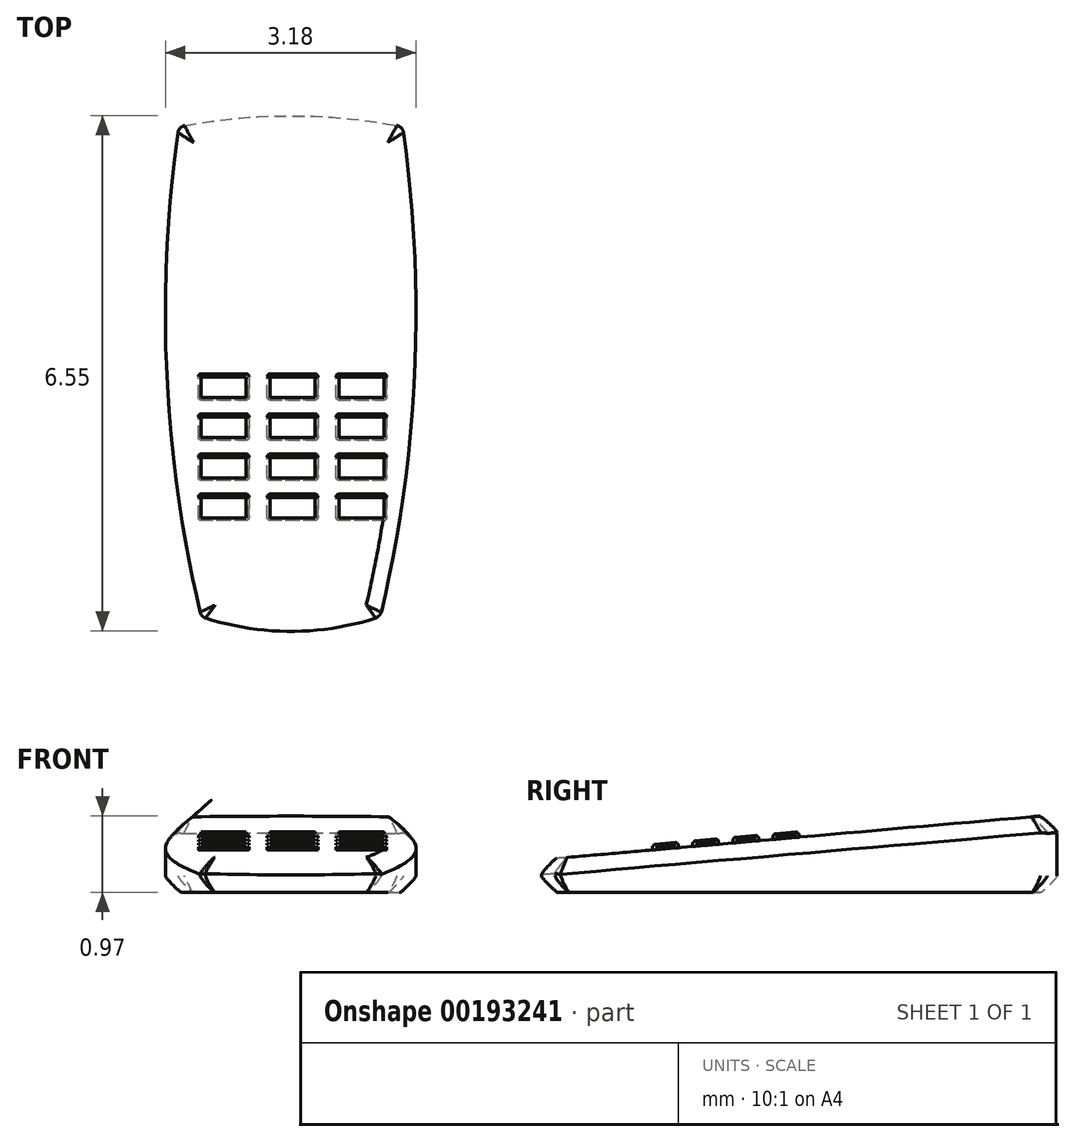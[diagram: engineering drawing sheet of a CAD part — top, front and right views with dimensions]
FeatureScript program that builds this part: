
annotation { "Feature Type Name" : "Feature", "Feature Type Description" : "" }
export const myFeature = defineFeature(function(context is Context, id is Id, definition is map)
    precondition{}
    {
        {
            var Q0;
            Q0=qCreatedBy(makeId("Top.planeOp"),FACE);
            var sketch = newSketch(context, id + "F0", { "sketchPlane" : qUnion([Q0])});
            skPoint(sketch, "E0", {"position": v(-40.64, 114.48) * mm});
            skPoint(sketch, "E1", {"position": v(-32.5, -63.32) * mm});
            skPoint(sketch, "E2.MirrorP", {"position": v(40.64, 114.48) * mm});
            skPoint(sketch, "E3.MirrorP", {"position": v(32.5, -63.32) * mm});
            skArc(sketch, "E4", {"start": v(38.52, 114.88) * mm, "mid": v(0, 118.42) * mm, "end": v(-38.52, 114.88) * mm});
            skArc(sketch, "E5", {"start": v(-40.94, 112.35) * mm, "mid": v(-45, 24.95) * mm, "end": v(-32.89, -61.7) * mm});
            skArc(sketch, "E6", {"start": v(-30.9, -63.86) * mm, "mid": v(0, -68.73) * mm, "end": v(30.9, -63.86) * mm});
            skArc(sketch, "E7.MirrorCS", {"start": v(40.94, 112.35) * mm, "mid": v(45, 24.95) * mm, "end": v(32.89, -61.7) * mm});
            skArc(sketch, "E8.filletArc", {"start": v(-38.52, 114.88) * mm, "mid": v(-40.14, 114) * mm, "end": v(-40.94, 112.35) * mm});
            skArc(sketch, "E9.filletArc", {"start": v(40.94, 112.35) * mm, "mid": v(40.14, 114) * mm, "end": v(38.52, 114.88) * mm});
            skArc(sketch, "E10.filletArc", {"start": v(-32.89, -61.7) * mm, "mid": v(-32.17, -63.04) * mm, "end": v(-30.9, -63.86) * mm});
            skArc(sketch, "E11.filletArc", {"start": v(30.9, -63.86) * mm, "mid": v(32.17, -63.04) * mm, "end": v(32.89, -61.7) * mm});
            skSolve(sketch);
        }
        {
            var Q0;
            Q0=qCreatedBy(makeId("Front.planeOp"),FACE);
            var sketch = newSketch(context, id + "F1", { "sketchPlane" : qUnion([Q0])});
            skLineSegment(sketch, "E12", {"start": v(-58.06, 17.9) * mm, "end": v(59.88, 17.9) * mm, "construction": true});
            skSolve(sketch);
        }
        {
            var Q0;
            Q0=sQuery(id+"F1.wireOp",EDGE,"E12");
            var Q1;
            Q1=qCreatedBy(makeId("Top.planeOp"),FACE);
            cPlane(context, id + "F2", {"entities" : qUnion([Q0, Q1]), "cplaneType" : CPlaneType.LINE_ANGLE, "offset" : 150 * mm, "angle" : 5 * degree, "width" : 150 * mm, "height" : 150 * mm});
        }
        {
            var Q0;
            Q0=makeQuery(id+"F0.imprint","IMPRINT",FACE,{"disambiguationData":[TD([[makeQuery(id+"F0.imprint","IMPRINT",EDGE,{"derivedFrom":sQuery(id+"F0.wireOp",EDGE,"E4")}),1.0]])]});
            var Q1;
            Q1=qCreatedBy(id+"F2.planeOp",FACE);
            extrude(context, id + "F3", {"entities" : qUnion([Q0]), "endBound" : BoundingType.UP_TO_SURFACE, "endBoundEntityFace" : qUnion([Q1]), "depth" : 25 * mm});
        }
        {
            var Q0;
            Q0=makeQuery(id+"F3.opExtrude","CAP_FACE",FACE,{"disambiguationData":[OSD([sQuery(id+"F0.wireOp",EDGE,"E4"),sQuery(id+"F0.wireOp",EDGE,"E5"),sQuery(id+"F0.wireOp",EDGE,"E6"),sQuery(id+"F0.wireOp",EDGE,"E7.MirrorCS"),sQuery(id+"F0.wireOp",EDGE,"E8.filletArc"),sQuery(id+"F0.wireOp",EDGE,"E9.filletArc"),sQuery(id+"F0.wireOp",EDGE,"E10.filletArc"),sQuery(id+"F0.wireOp",EDGE,"E11.filletArc")])],"isStart":false});
            var Q1;
            Q1=makeQuery(id+"F3.opExtrude","CAP_FACE",FACE,{"disambiguationData":[OSD([sQuery(id+"F0.wireOp",EDGE,"E4"),sQuery(id+"F0.wireOp",EDGE,"E5"),sQuery(id+"F0.wireOp",EDGE,"E6"),sQuery(id+"F0.wireOp",EDGE,"E7.MirrorCS"),sQuery(id+"F0.wireOp",EDGE,"E8.filletArc"),sQuery(id+"F0.wireOp",EDGE,"E9.filletArc"),sQuery(id+"F0.wireOp",EDGE,"E10.filletArc"),sQuery(id+"F0.wireOp",EDGE,"E11.filletArc")])],"isStart":true});
            fillet(context, id + "F4", {"entities" : qUnion([Q0, Q1]), "radius" : 6 * mm, "tangentPropagation" : true, "rho" : .1, "crossSection" : FilletCrossSection.CONIC, "allowEdgeOverflow" : false});
        }
        {
            var Q0;
            Q0=makeQuery(id+"F3.opExtrude","CAP_FACE",FACE,{"disambiguationData":[OSD([sQuery(id+"F0.wireOp",EDGE,"E4"),sQuery(id+"F0.wireOp",EDGE,"E5"),sQuery(id+"F0.wireOp",EDGE,"E6"),sQuery(id+"F0.wireOp",EDGE,"E7.MirrorCS"),sQuery(id+"F0.wireOp",EDGE,"E8.filletArc"),sQuery(id+"F0.wireOp",EDGE,"E9.filletArc"),sQuery(id+"F0.wireOp",EDGE,"E10.filletArc"),sQuery(id+"F0.wireOp",EDGE,"E11.filletArc")])],"isStart":false});
            var sketch = newSketch(context, id + "F5", { "sketchPlane" : qUnion([Q0])});
            skLineSegment(sketch, "E13.bottom", {"start": v(-32.5, 16.97) * mm, "end": v(-16.15, 16.97) * mm});
            skLineSegment(sketch, "E13.top", {"start": v(-32.5, 26.44) * mm, "end": v(-16.15, 26.44) * mm});
            skLineSegment(sketch, "E13.left", {"start": v(-33.5, 17.97) * mm, "end": v(-33.5, 25.44) * mm});
            skLineSegment(sketch, "E13.right", {"start": v(-15.15, 17.97) * mm, "end": v(-15.15, 25.44) * mm});
            skPoint(sketch, "E14.visualSharp", {"position": v(-33.5, 26.44) * mm});
            skArc(sketch, "E14.filletArc", {"start": v(-32.5, 26.44) * mm, "mid": v(-33.2, 26.15) * mm, "end": v(-33.5, 25.44) * mm});
            skPoint(sketch, "E15.visualSharp", {"position": v(-15.15, 26.44) * mm});
            skArc(sketch, "E15.filletArc", {"start": v(-15.15, 25.44) * mm, "mid": v(-15.44, 26.15) * mm, "end": v(-16.15, 26.44) * mm});
            skPoint(sketch, "E16.visualSharp", {"position": v(-15.15, 16.97) * mm});
            skArc(sketch, "E16.filletArc", {"start": v(-16.15, 16.97) * mm, "mid": v(-15.44, 17.26) * mm, "end": v(-15.15, 17.97) * mm});
            skPoint(sketch, "E17.visualSharp", {"position": v(-33.5, 16.97) * mm});
            skArc(sketch, "E17.filletArc", {"start": v(-33.5, 17.97) * mm, "mid": v(-33.2, 17.26) * mm, "end": v(-32.5, 16.97) * mm});
            skLineSegment(sketch, "E18.0.1.0", {"start": v(-33.5, 3.35) * mm, "end": v(-33.5, 10.82) * mm});
            skPoint(sketch, "E18.0.1.1", {"position": v(-15.15, 2.35) * mm});
            skLineSegment(sketch, "E18.0.1.2", {"start": v(-15.15, 3.35) * mm, "end": v(-15.15, 10.82) * mm});
            skPoint(sketch, "E18.0.1.3", {"position": v(-33.5, 11.82) * mm});
            skLineSegment(sketch, "E18.0.1.4", {"start": v(-32.5, 2.35) * mm, "end": v(-16.15, 2.35) * mm});
            skPoint(sketch, "E18.0.1.5", {"position": v(-15.15, 11.82) * mm});
            skLineSegment(sketch, "E18.0.1.6", {"start": v(-32.5, 11.82) * mm, "end": v(-16.15, 11.82) * mm});
            skPoint(sketch, "E18.0.1.7", {"position": v(-33.5, 2.35) * mm});
            skArc(sketch, "E18.0.1.8", {"start": v(-33.5, 3.35) * mm, "mid": v(-33.2, 2.65) * mm, "end": v(-32.5, 2.35) * mm});
            skArc(sketch, "E18.0.1.9", {"start": v(-15.15, 10.82) * mm, "mid": v(-15.44, 11.53) * mm, "end": v(-16.15, 11.82) * mm});
            skArc(sketch, "E18.0.1.10", {"start": v(-16.15, 2.35) * mm, "mid": v(-15.44, 2.65) * mm, "end": v(-15.15, 3.35) * mm});
            skArc(sketch, "E18.0.1.11", {"start": v(-32.5, 11.82) * mm, "mid": v(-33.2, 11.53) * mm, "end": v(-33.5, 10.82) * mm});
            skLineSegment(sketch, "E18.0.2.0", {"start": v(-33.5, -11.27) * mm, "end": v(-33.5, -3.8) * mm});
            skPoint(sketch, "E18.0.2.1", {"position": v(-15.15, -12.27) * mm});
            skLineSegment(sketch, "E18.0.2.2", {"start": v(-15.15, -11.27) * mm, "end": v(-15.15, -3.8) * mm});
            skPoint(sketch, "E18.0.2.3", {"position": v(-33.5, -2.8) * mm});
            skLineSegment(sketch, "E18.0.2.4", {"start": v(-32.5, -12.27) * mm, "end": v(-16.15, -12.27) * mm});
            skPoint(sketch, "E18.0.2.5", {"position": v(-15.15, -2.8) * mm});
            skLineSegment(sketch, "E18.0.2.6", {"start": v(-32.5, -2.8) * mm, "end": v(-16.15, -2.8) * mm});
            skPoint(sketch, "E18.0.2.7", {"position": v(-33.5, -12.27) * mm});
            skArc(sketch, "E18.0.2.8", {"start": v(-33.5, -11.27) * mm, "mid": v(-33.2, -11.97) * mm, "end": v(-32.5, -12.27) * mm});
            skArc(sketch, "E18.0.2.9", {"start": v(-15.15, -3.8) * mm, "mid": v(-15.44, -3.09) * mm, "end": v(-16.15, -2.8) * mm});
            skArc(sketch, "E18.0.2.10", {"start": v(-16.15, -12.27) * mm, "mid": v(-15.44, -11.97) * mm, "end": v(-15.15, -11.27) * mm});
            skArc(sketch, "E18.0.2.11", {"start": v(-32.5, -2.8) * mm, "mid": v(-33.2, -3.09) * mm, "end": v(-33.5, -3.8) * mm});
            skLineSegment(sketch, "E18.0.3.0", {"start": v(-33.5, -25.89) * mm, "end": v(-33.5, -18.41) * mm});
            skPoint(sketch, "E18.0.3.1", {"position": v(-15.15, -26.89) * mm});
            skLineSegment(sketch, "E18.0.3.2", {"start": v(-15.15, -25.89) * mm, "end": v(-15.15, -18.41) * mm});
            skPoint(sketch, "E18.0.3.3", {"position": v(-33.5, -17.41) * mm});
            skLineSegment(sketch, "E18.0.3.4", {"start": v(-32.5, -26.89) * mm, "end": v(-16.15, -26.89) * mm});
            skPoint(sketch, "E18.0.3.5", {"position": v(-15.15, -17.41) * mm});
            skLineSegment(sketch, "E18.0.3.6", {"start": v(-32.5, -17.41) * mm, "end": v(-16.15, -17.41) * mm});
            skPoint(sketch, "E18.0.3.7", {"position": v(-33.5, -26.89) * mm});
            skArc(sketch, "E18.0.3.8", {"start": v(-33.5, -25.89) * mm, "mid": v(-33.2, -26.6) * mm, "end": v(-32.5, -26.89) * mm});
            skArc(sketch, "E18.0.3.9", {"start": v(-15.15, -18.41) * mm, "mid": v(-15.44, -17.7) * mm, "end": v(-16.15, -17.41) * mm});
            skArc(sketch, "E18.0.3.10", {"start": v(-16.15, -26.89) * mm, "mid": v(-15.44, -26.6) * mm, "end": v(-15.15, -25.89) * mm});
            skArc(sketch, "E18.0.3.11", {"start": v(-32.5, -17.41) * mm, "mid": v(-33.2, -17.7) * mm, "end": v(-33.5, -18.41) * mm});
            skLineSegment(sketch, "E18.1.0.0", {"start": v(-8.5, 17.97) * mm, "end": v(-8.5, 25.44) * mm});
            skPoint(sketch, "E18.1.0.1", {"position": v(9.85, 16.97) * mm});
            skLineSegment(sketch, "E18.1.0.2", {"start": v(9.85, 17.97) * mm, "end": v(9.85, 25.44) * mm});
            skPoint(sketch, "E18.1.0.3", {"position": v(-8.5, 26.44) * mm});
            skLineSegment(sketch, "E18.1.0.4", {"start": v(-7.5, 16.97) * mm, "end": v(8.85, 16.97) * mm});
            skPoint(sketch, "E18.1.0.5", {"position": v(9.85, 26.44) * mm});
            skLineSegment(sketch, "E18.1.0.6", {"start": v(-7.5, 26.44) * mm, "end": v(8.85, 26.44) * mm});
            skPoint(sketch, "E18.1.0.7", {"position": v(-8.5, 16.97) * mm});
            skArc(sketch, "E18.1.0.8", {"start": v(-8.5, 17.97) * mm, "mid": v(-8.2, 17.26) * mm, "end": v(-7.5, 16.97) * mm});
            skArc(sketch, "E18.1.0.9", {"start": v(9.85, 25.44) * mm, "mid": v(9.56, 26.15) * mm, "end": v(8.85, 26.44) * mm});
            skArc(sketch, "E18.1.0.10", {"start": v(8.85, 16.97) * mm, "mid": v(9.56, 17.26) * mm, "end": v(9.85, 17.97) * mm});
            skArc(sketch, "E18.1.0.11", {"start": v(-7.5, 26.44) * mm, "mid": v(-8.2, 26.15) * mm, "end": v(-8.5, 25.44) * mm});
            skLineSegment(sketch, "E18.1.1.0", {"start": v(-8.5, 3.35) * mm, "end": v(-8.5, 10.82) * mm});
            skPoint(sketch, "E18.1.1.1", {"position": v(9.85, 2.35) * mm});
            skLineSegment(sketch, "E18.1.1.2", {"start": v(9.85, 3.35) * mm, "end": v(9.85, 10.82) * mm});
            skPoint(sketch, "E18.1.1.3", {"position": v(-8.5, 11.82) * mm});
            skLineSegment(sketch, "E18.1.1.4", {"start": v(-7.5, 2.35) * mm, "end": v(8.85, 2.35) * mm});
            skPoint(sketch, "E18.1.1.5", {"position": v(9.85, 11.82) * mm});
            skLineSegment(sketch, "E18.1.1.6", {"start": v(-7.5, 11.82) * mm, "end": v(8.85, 11.82) * mm});
            skPoint(sketch, "E18.1.1.7", {"position": v(-8.5, 2.35) * mm});
            skArc(sketch, "E18.1.1.8", {"start": v(-8.5, 3.35) * mm, "mid": v(-8.2, 2.65) * mm, "end": v(-7.5, 2.35) * mm});
            skArc(sketch, "E18.1.1.9", {"start": v(9.85, 10.82) * mm, "mid": v(9.56, 11.53) * mm, "end": v(8.85, 11.82) * mm});
            skArc(sketch, "E18.1.1.10", {"start": v(8.85, 2.35) * mm, "mid": v(9.56, 2.65) * mm, "end": v(9.85, 3.35) * mm});
            skArc(sketch, "E18.1.1.11", {"start": v(-7.5, 11.82) * mm, "mid": v(-8.2, 11.53) * mm, "end": v(-8.5, 10.82) * mm});
            skLineSegment(sketch, "E18.1.2.0", {"start": v(-8.5, -11.27) * mm, "end": v(-8.5, -3.8) * mm});
            skPoint(sketch, "E18.1.2.1", {"position": v(9.85, -12.27) * mm});
            skLineSegment(sketch, "E18.1.2.2", {"start": v(9.85, -11.27) * mm, "end": v(9.85, -3.8) * mm});
            skPoint(sketch, "E18.1.2.3", {"position": v(-8.5, -2.8) * mm});
            skLineSegment(sketch, "E18.1.2.4", {"start": v(-7.5, -12.27) * mm, "end": v(8.85, -12.27) * mm});
            skPoint(sketch, "E18.1.2.5", {"position": v(9.85, -2.8) * mm});
            skLineSegment(sketch, "E18.1.2.6", {"start": v(-7.5, -2.8) * mm, "end": v(8.85, -2.8) * mm});
            skPoint(sketch, "E18.1.2.7", {"position": v(-8.5, -12.27) * mm});
            skArc(sketch, "E18.1.2.8", {"start": v(-8.5, -11.27) * mm, "mid": v(-8.2, -11.97) * mm, "end": v(-7.5, -12.27) * mm});
            skArc(sketch, "E18.1.2.9", {"start": v(9.85, -3.8) * mm, "mid": v(9.56, -3.09) * mm, "end": v(8.85, -2.8) * mm});
            skArc(sketch, "E18.1.2.10", {"start": v(8.85, -12.27) * mm, "mid": v(9.56, -11.97) * mm, "end": v(9.85, -11.27) * mm});
            skArc(sketch, "E18.1.2.11", {"start": v(-7.5, -2.8) * mm, "mid": v(-8.2, -3.09) * mm, "end": v(-8.5, -3.8) * mm});
            skLineSegment(sketch, "E18.1.3.0", {"start": v(-8.5, -25.89) * mm, "end": v(-8.5, -18.41) * mm});
            skPoint(sketch, "E18.1.3.1", {"position": v(9.85, -26.89) * mm});
            skLineSegment(sketch, "E18.1.3.2", {"start": v(9.85, -25.89) * mm, "end": v(9.85, -18.41) * mm});
            skPoint(sketch, "E18.1.3.3", {"position": v(-8.5, -17.41) * mm});
            skLineSegment(sketch, "E18.1.3.4", {"start": v(-7.5, -26.89) * mm, "end": v(8.85, -26.89) * mm});
            skPoint(sketch, "E18.1.3.5", {"position": v(9.85, -17.41) * mm});
            skLineSegment(sketch, "E18.1.3.6", {"start": v(-7.5, -17.41) * mm, "end": v(8.85, -17.41) * mm});
            skPoint(sketch, "E18.1.3.7", {"position": v(-8.5, -26.89) * mm});
            skArc(sketch, "E18.1.3.8", {"start": v(-8.5, -25.89) * mm, "mid": v(-8.2, -26.6) * mm, "end": v(-7.5, -26.89) * mm});
            skArc(sketch, "E18.1.3.9", {"start": v(9.85, -18.41) * mm, "mid": v(9.56, -17.7) * mm, "end": v(8.85, -17.41) * mm});
            skArc(sketch, "E18.1.3.10", {"start": v(8.85, -26.89) * mm, "mid": v(9.56, -26.6) * mm, "end": v(9.85, -25.89) * mm});
            skArc(sketch, "E18.1.3.11", {"start": v(-7.5, -17.41) * mm, "mid": v(-8.2, -17.7) * mm, "end": v(-8.5, -18.41) * mm});
            skLineSegment(sketch, "E18.2.0.0", {"start": v(16.5, 17.97) * mm, "end": v(16.5, 25.44) * mm});
            skPoint(sketch, "E18.2.0.1", {"position": v(34.85, 16.97) * mm});
            skLineSegment(sketch, "E18.2.0.2", {"start": v(34.85, 17.97) * mm, "end": v(34.85, 25.44) * mm});
            skPoint(sketch, "E18.2.0.3", {"position": v(16.5, 26.44) * mm});
            skLineSegment(sketch, "E18.2.0.4", {"start": v(17.5, 16.97) * mm, "end": v(33.85, 16.97) * mm});
            skPoint(sketch, "E18.2.0.5", {"position": v(34.85, 26.44) * mm});
            skLineSegment(sketch, "E18.2.0.6", {"start": v(17.5, 26.44) * mm, "end": v(33.85, 26.44) * mm});
            skPoint(sketch, "E18.2.0.7", {"position": v(16.5, 16.97) * mm});
            skArc(sketch, "E18.2.0.8", {"start": v(16.5, 17.97) * mm, "mid": v(16.8, 17.26) * mm, "end": v(17.5, 16.97) * mm});
            skArc(sketch, "E18.2.0.9", {"start": v(34.85, 25.44) * mm, "mid": v(34.56, 26.15) * mm, "end": v(33.85, 26.44) * mm});
            skArc(sketch, "E18.2.0.10", {"start": v(33.85, 16.97) * mm, "mid": v(34.56, 17.26) * mm, "end": v(34.85, 17.97) * mm});
            skArc(sketch, "E18.2.0.11", {"start": v(17.5, 26.44) * mm, "mid": v(16.8, 26.15) * mm, "end": v(16.5, 25.44) * mm});
            skLineSegment(sketch, "E18.2.1.0", {"start": v(16.5, 3.35) * mm, "end": v(16.5, 10.82) * mm});
            skPoint(sketch, "E18.2.1.1", {"position": v(34.85, 2.35) * mm});
            skLineSegment(sketch, "E18.2.1.2", {"start": v(34.85, 3.35) * mm, "end": v(34.85, 10.82) * mm});
            skPoint(sketch, "E18.2.1.3", {"position": v(16.5, 11.82) * mm});
            skLineSegment(sketch, "E18.2.1.4", {"start": v(17.5, 2.35) * mm, "end": v(33.85, 2.35) * mm});
            skPoint(sketch, "E18.2.1.5", {"position": v(34.85, 11.82) * mm});
            skLineSegment(sketch, "E18.2.1.6", {"start": v(17.5, 11.82) * mm, "end": v(33.85, 11.82) * mm});
            skPoint(sketch, "E18.2.1.7", {"position": v(16.5, 2.35) * mm});
            skArc(sketch, "E18.2.1.8", {"start": v(16.5, 3.35) * mm, "mid": v(16.8, 2.65) * mm, "end": v(17.5, 2.35) * mm});
            skArc(sketch, "E18.2.1.9", {"start": v(34.85, 10.82) * mm, "mid": v(34.56, 11.53) * mm, "end": v(33.85, 11.82) * mm});
            skArc(sketch, "E18.2.1.10", {"start": v(33.85, 2.35) * mm, "mid": v(34.56, 2.65) * mm, "end": v(34.85, 3.35) * mm});
            skArc(sketch, "E18.2.1.11", {"start": v(17.5, 11.82) * mm, "mid": v(16.8, 11.53) * mm, "end": v(16.5, 10.82) * mm});
            skLineSegment(sketch, "E18.2.2.0", {"start": v(16.5, -11.27) * mm, "end": v(16.5, -3.8) * mm});
            skPoint(sketch, "E18.2.2.1", {"position": v(34.85, -12.27) * mm});
            skLineSegment(sketch, "E18.2.2.2", {"start": v(34.85, -11.27) * mm, "end": v(34.85, -3.8) * mm});
            skPoint(sketch, "E18.2.2.3", {"position": v(16.5, -2.8) * mm});
            skLineSegment(sketch, "E18.2.2.4", {"start": v(17.5, -12.27) * mm, "end": v(33.85, -12.27) * mm});
            skPoint(sketch, "E18.2.2.5", {"position": v(34.85, -2.8) * mm});
            skLineSegment(sketch, "E18.2.2.6", {"start": v(17.5, -2.8) * mm, "end": v(33.85, -2.8) * mm});
            skPoint(sketch, "E18.2.2.7", {"position": v(16.5, -12.27) * mm});
            skArc(sketch, "E18.2.2.8", {"start": v(16.5, -11.27) * mm, "mid": v(16.8, -11.97) * mm, "end": v(17.5, -12.27) * mm});
            skArc(sketch, "E18.2.2.9", {"start": v(34.85, -3.8) * mm, "mid": v(34.56, -3.09) * mm, "end": v(33.85, -2.8) * mm});
            skArc(sketch, "E18.2.2.10", {"start": v(33.85, -12.27) * mm, "mid": v(34.56, -11.97) * mm, "end": v(34.85, -11.27) * mm});
            skArc(sketch, "E18.2.2.11", {"start": v(17.5, -2.8) * mm, "mid": v(16.8, -3.09) * mm, "end": v(16.5, -3.8) * mm});
            skLineSegment(sketch, "E18.2.3.0", {"start": v(16.5, -25.89) * mm, "end": v(16.5, -18.41) * mm});
            skPoint(sketch, "E18.2.3.1", {"position": v(34.85, -26.89) * mm});
            skLineSegment(sketch, "E18.2.3.2", {"start": v(34.85, -25.89) * mm, "end": v(34.85, -18.41) * mm});
            skPoint(sketch, "E18.2.3.3", {"position": v(16.5, -17.41) * mm});
            skLineSegment(sketch, "E18.2.3.4", {"start": v(17.5, -26.89) * mm, "end": v(33.85, -26.89) * mm});
            skPoint(sketch, "E18.2.3.5", {"position": v(34.85, -17.41) * mm});
            skLineSegment(sketch, "E18.2.3.6", {"start": v(17.5, -17.41) * mm, "end": v(33.85, -17.41) * mm});
            skPoint(sketch, "E18.2.3.7", {"position": v(16.5, -26.89) * mm});
            skArc(sketch, "E18.2.3.8", {"start": v(16.5, -25.89) * mm, "mid": v(16.8, -26.6) * mm, "end": v(17.5, -26.89) * mm});
            skArc(sketch, "E18.2.3.9", {"start": v(34.85, -18.41) * mm, "mid": v(34.56, -17.7) * mm, "end": v(33.85, -17.41) * mm});
            skArc(sketch, "E18.2.3.10", {"start": v(33.85, -26.89) * mm, "mid": v(34.56, -26.6) * mm, "end": v(34.85, -25.89) * mm});
            skArc(sketch, "E18.2.3.11", {"start": v(17.5, -17.41) * mm, "mid": v(16.8, -17.7) * mm, "end": v(16.5, -18.41) * mm});
            skLineSegment(sketch, "E18.direction1", {"start": v(-33.5, 17.97) * mm, "end": v(-8.5, 17.97) * mm, "construction": true});
            skLineSegment(sketch, "E18.direction2", {"start": v(-33.5, 17.97) * mm, "end": v(-33.5, 3.35) * mm, "construction": true});
            skSolve(sketch);
        }
        {
            var Q0;
            Q0=qSketchRegion(id+"F5",true);
            extrude(context, id + "F6", {"entities" : qUnion([Q0]), "operationType" : NewBodyOperationType.ADD, "depth" : 2 * mm});
        }
        {
            var Q0;
            Q0=makeQuery(id+"F6.opExtrude","CAP_FACE",FACE,{"disambiguationData":[OSD([sQuery(id+"F5.wireOp",EDGE,"E13.bottom"),sQuery(id+"F5.wireOp",EDGE,"E13.top"),sQuery(id+"F5.wireOp",EDGE,"E13.left"),sQuery(id+"F5.wireOp",EDGE,"E13.right"),sQuery(id+"F5.wireOp",EDGE,"E14.filletArc"),sQuery(id+"F5.wireOp",EDGE,"E15.filletArc"),sQuery(id+"F5.wireOp",EDGE,"E16.filletArc"),sQuery(id+"F5.wireOp",EDGE,"E17.filletArc")])],"isStart":false});
            var Q1;
            Q1=makeQuery(id+"F6.opExtrude","CAP_FACE",FACE,{"disambiguationData":[OSD([sQuery(id+"F5.wireOp",EDGE,"E18.1.0.0"),sQuery(id+"F5.wireOp",EDGE,"E18.1.0.2"),sQuery(id+"F5.wireOp",EDGE,"E18.1.0.4"),sQuery(id+"F5.wireOp",EDGE,"E18.1.0.6"),sQuery(id+"F5.wireOp",EDGE,"E18.1.0.8"),sQuery(id+"F5.wireOp",EDGE,"E18.1.0.9"),sQuery(id+"F5.wireOp",EDGE,"E18.1.0.10"),sQuery(id+"F5.wireOp",EDGE,"E18.1.0.11")])],"isStart":false});
            var Q2;
            Q2=makeQuery(id+"F6.opExtrude","CAP_FACE",FACE,{"disambiguationData":[OSD([sQuery(id+"F5.wireOp",EDGE,"E18.2.0.0"),sQuery(id+"F5.wireOp",EDGE,"E18.2.0.2"),sQuery(id+"F5.wireOp",EDGE,"E18.2.0.4"),sQuery(id+"F5.wireOp",EDGE,"E18.2.0.6"),sQuery(id+"F5.wireOp",EDGE,"E18.2.0.8"),sQuery(id+"F5.wireOp",EDGE,"E18.2.0.9"),sQuery(id+"F5.wireOp",EDGE,"E18.2.0.10"),sQuery(id+"F5.wireOp",EDGE,"E18.2.0.11")])],"isStart":false});
            var Q3;
            Q3=makeQuery(id+"F6.opExtrude","CAP_FACE",FACE,{"disambiguationData":[OSD([sQuery(id+"F5.wireOp",EDGE,"E18.2.1.0"),sQuery(id+"F5.wireOp",EDGE,"E18.2.1.2"),sQuery(id+"F5.wireOp",EDGE,"E18.2.1.4"),sQuery(id+"F5.wireOp",EDGE,"E18.2.1.6"),sQuery(id+"F5.wireOp",EDGE,"E18.2.1.8"),sQuery(id+"F5.wireOp",EDGE,"E18.2.1.9"),sQuery(id+"F5.wireOp",EDGE,"E18.2.1.10"),sQuery(id+"F5.wireOp",EDGE,"E18.2.1.11")])],"isStart":false});
            var Q4;
            Q4=makeQuery(id+"F6.opExtrude","CAP_FACE",FACE,{"disambiguationData":[OSD([sQuery(id+"F5.wireOp",EDGE,"E18.1.1.0"),sQuery(id+"F5.wireOp",EDGE,"E18.1.1.2"),sQuery(id+"F5.wireOp",EDGE,"E18.1.1.4"),sQuery(id+"F5.wireOp",EDGE,"E18.1.1.6"),sQuery(id+"F5.wireOp",EDGE,"E18.1.1.8"),sQuery(id+"F5.wireOp",EDGE,"E18.1.1.9"),sQuery(id+"F5.wireOp",EDGE,"E18.1.1.10"),sQuery(id+"F5.wireOp",EDGE,"E18.1.1.11")])],"isStart":false});
            var Q5;
            Q5=makeQuery(id+"F6.opExtrude","CAP_FACE",FACE,{"disambiguationData":[OSD([sQuery(id+"F5.wireOp",EDGE,"E18.0.1.0"),sQuery(id+"F5.wireOp",EDGE,"E18.0.1.2"),sQuery(id+"F5.wireOp",EDGE,"E18.0.1.4"),sQuery(id+"F5.wireOp",EDGE,"E18.0.1.6"),sQuery(id+"F5.wireOp",EDGE,"E18.0.1.8"),sQuery(id+"F5.wireOp",EDGE,"E18.0.1.9"),sQuery(id+"F5.wireOp",EDGE,"E18.0.1.10"),sQuery(id+"F5.wireOp",EDGE,"E18.0.1.11")])],"isStart":false});
            var Q6;
            Q6=makeQuery(id+"F6.opExtrude","CAP_FACE",FACE,{"disambiguationData":[OSD([sQuery(id+"F5.wireOp",EDGE,"E18.0.2.0"),sQuery(id+"F5.wireOp",EDGE,"E18.0.2.2"),sQuery(id+"F5.wireOp",EDGE,"E18.0.2.4"),sQuery(id+"F5.wireOp",EDGE,"E18.0.2.6"),sQuery(id+"F5.wireOp",EDGE,"E18.0.2.8"),sQuery(id+"F5.wireOp",EDGE,"E18.0.2.9"),sQuery(id+"F5.wireOp",EDGE,"E18.0.2.10"),sQuery(id+"F5.wireOp",EDGE,"E18.0.2.11")])],"isStart":false});
            var Q7;
            Q7=makeQuery(id+"F6.opExtrude","CAP_FACE",FACE,{"disambiguationData":[OSD([sQuery(id+"F5.wireOp",EDGE,"E18.1.2.0"),sQuery(id+"F5.wireOp",EDGE,"E18.1.2.2"),sQuery(id+"F5.wireOp",EDGE,"E18.1.2.4"),sQuery(id+"F5.wireOp",EDGE,"E18.1.2.6"),sQuery(id+"F5.wireOp",EDGE,"E18.1.2.8"),sQuery(id+"F5.wireOp",EDGE,"E18.1.2.9"),sQuery(id+"F5.wireOp",EDGE,"E18.1.2.10"),sQuery(id+"F5.wireOp",EDGE,"E18.1.2.11")])],"isStart":false});
            var Q8;
            Q8=makeQuery(id+"F6.opExtrude","CAP_FACE",FACE,{"disambiguationData":[OSD([sQuery(id+"F5.wireOp",EDGE,"E18.2.2.0"),sQuery(id+"F5.wireOp",EDGE,"E18.2.2.2"),sQuery(id+"F5.wireOp",EDGE,"E18.2.2.4"),sQuery(id+"F5.wireOp",EDGE,"E18.2.2.6"),sQuery(id+"F5.wireOp",EDGE,"E18.2.2.8"),sQuery(id+"F5.wireOp",EDGE,"E18.2.2.9"),sQuery(id+"F5.wireOp",EDGE,"E18.2.2.10"),sQuery(id+"F5.wireOp",EDGE,"E18.2.2.11")])],"isStart":false});
            var Q9;
            Q9=makeQuery(id+"F6.opExtrude","CAP_FACE",FACE,{"disambiguationData":[OSD([sQuery(id+"F5.wireOp",EDGE,"E18.2.3.0"),sQuery(id+"F5.wireOp",EDGE,"E18.2.3.2"),sQuery(id+"F5.wireOp",EDGE,"E18.2.3.4"),sQuery(id+"F5.wireOp",EDGE,"E18.2.3.6"),sQuery(id+"F5.wireOp",EDGE,"E18.2.3.8"),sQuery(id+"F5.wireOp",EDGE,"E18.2.3.9"),sQuery(id+"F5.wireOp",EDGE,"E18.2.3.10"),sQuery(id+"F5.wireOp",EDGE,"E18.2.3.11")])],"isStart":false});
            var Q10;
            Q10=makeQuery(id+"F6.opExtrude","CAP_FACE",FACE,{"disambiguationData":[OSD([sQuery(id+"F5.wireOp",EDGE,"E18.1.3.0"),sQuery(id+"F5.wireOp",EDGE,"E18.1.3.2"),sQuery(id+"F5.wireOp",EDGE,"E18.1.3.4"),sQuery(id+"F5.wireOp",EDGE,"E18.1.3.6"),sQuery(id+"F5.wireOp",EDGE,"E18.1.3.8"),sQuery(id+"F5.wireOp",EDGE,"E18.1.3.9"),sQuery(id+"F5.wireOp",EDGE,"E18.1.3.10"),sQuery(id+"F5.wireOp",EDGE,"E18.1.3.11")])],"isStart":false});
            var Q11;
            Q11=makeQuery(id+"F6.opExtrude","CAP_FACE",FACE,{"disambiguationData":[OSD([sQuery(id+"F5.wireOp",EDGE,"E18.0.3.0"),sQuery(id+"F5.wireOp",EDGE,"E18.0.3.2"),sQuery(id+"F5.wireOp",EDGE,"E18.0.3.4"),sQuery(id+"F5.wireOp",EDGE,"E18.0.3.6"),sQuery(id+"F5.wireOp",EDGE,"E18.0.3.8"),sQuery(id+"F5.wireOp",EDGE,"E18.0.3.9"),sQuery(id+"F5.wireOp",EDGE,"E18.0.3.10"),sQuery(id+"F5.wireOp",EDGE,"E18.0.3.11")])],"isStart":false});
            fillet(context, id + "F7", {"entities" : qUnion([Q0, Q1, Q2, Q3, Q4, Q5, Q6, Q7, Q8, Q9, Q10, Q11]), "radius" : 1 * mm, "tangentPropagation" : true, "rho" : .2, "crossSection" : FilletCrossSection.CONIC, "allowEdgeOverflow" : false});
        }
        {
            var Q0;
            Q0=makeQuery(id+"F3.opExtrude","CAP_FACE",FACE,{"disambiguationData":[OSD([sQuery(id+"F0.wireOp",EDGE,"E4"),sQuery(id+"F0.wireOp",EDGE,"E5"),sQuery(id+"F0.wireOp",EDGE,"E6"),sQuery(id+"F0.wireOp",EDGE,"E7.MirrorCS"),sQuery(id+"F0.wireOp",EDGE,"E8.filletArc"),sQuery(id+"F0.wireOp",EDGE,"E9.filletArc"),sQuery(id+"F0.wireOp",EDGE,"E10.filletArc"),sQuery(id+"F0.wireOp",EDGE,"E11.filletArc")])],"isStart":true});
            var sketch = newSketch(context, id + "F8", { "sketchPlane" : qUnion([Q0])});
            skPoint(sketch, "E19", {"position": v(0, -31.44) * mm});
            skSolve(sketch);
        }
        {
            var Q0;
            Q0=makeQuery(id+"F3.opExtrude","SWEPT_BODY",BODY,{"disambiguationData":[OSD([sQuery(id+"F0.wireOp",EDGE,"E4"),sQuery(id+"F0.wireOp",EDGE,"E5"),sQuery(id+"F0.wireOp",EDGE,"E6"),sQuery(id+"F0.wireOp",EDGE,"E7.MirrorCS"),sQuery(id+"F0.wireOp",EDGE,"E8.filletArc"),sQuery(id+"F0.wireOp",EDGE,"E9.filletArc"),sQuery(id+"F0.wireOp",EDGE,"E10.filletArc"),sQuery(id+"F0.wireOp",EDGE,"E11.filletArc")])]});
            var Q1;
            Q1=sQuery(id+"F8.wireOp",VERTEX,"E19");
            transform(context, id + "F9", {"entities" : qUnion([Q0]), "transformType" : TransformType.SCALE_UNIFORMLY, "scale" : 0.04, "scalePoint" : qUnion([Q1]), "makeCopy" : false});
        }
    });
